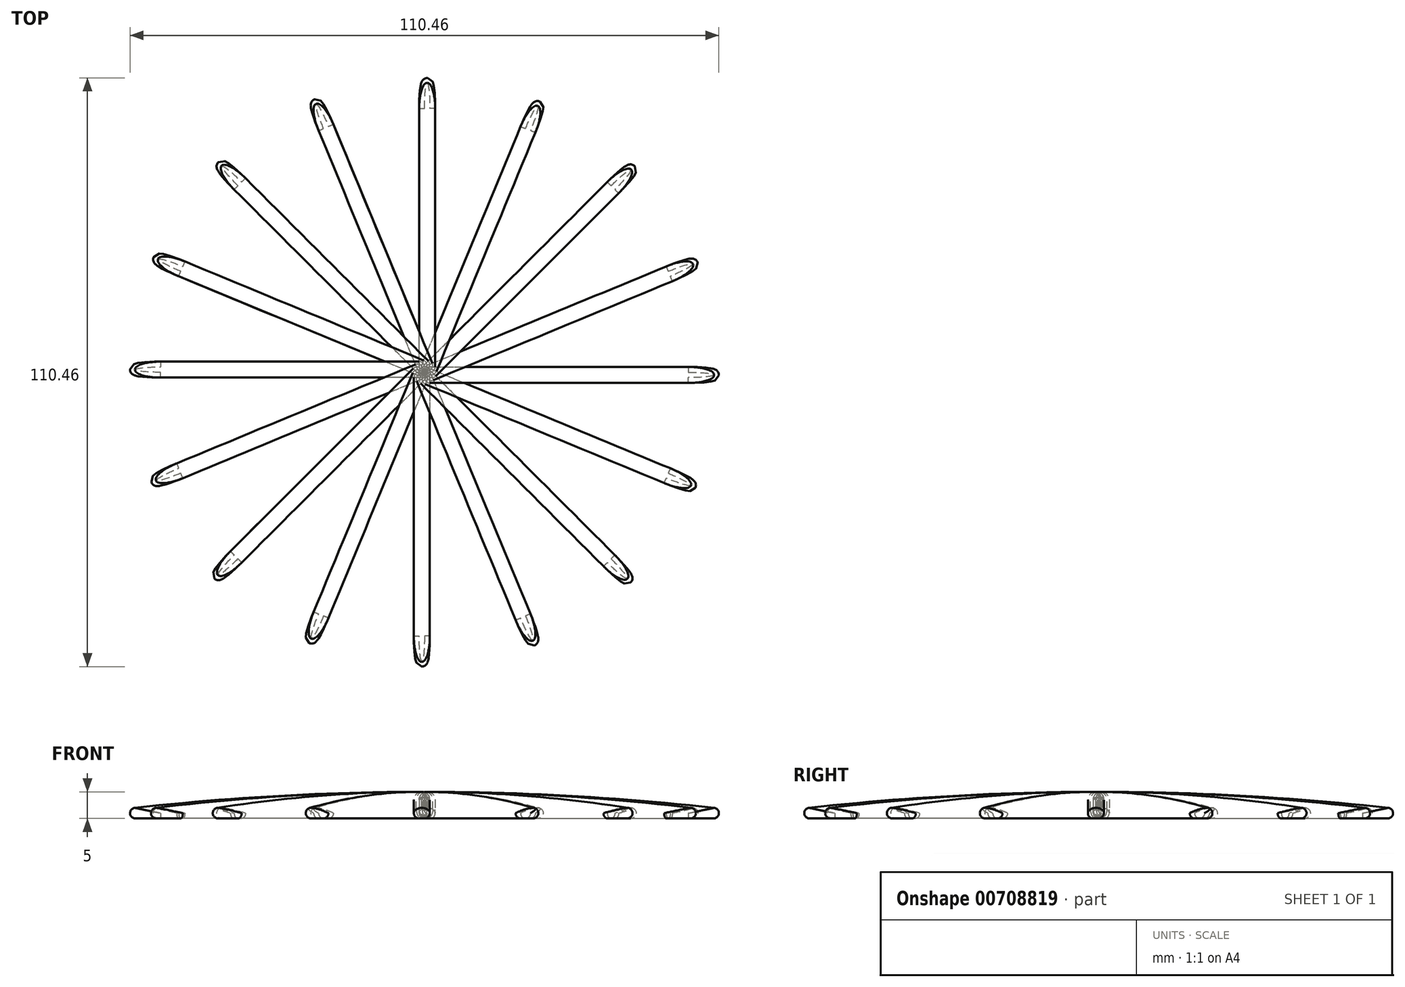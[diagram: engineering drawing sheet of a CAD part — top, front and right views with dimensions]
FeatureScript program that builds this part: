
annotation { "Feature Type Name" : "Feature", "Feature Type Description" : "" }
export const myFeature = defineFeature(function(context is Context, id is Id, definition is map)
    precondition{}
    {
        {
            var Q0;
            Q0=qCreatedBy(makeId("Top.planeOp"),FACE);
            var sketch = newSketch(context, id + "F0", { "sketchPlane" : qUnion([Q0])});
            skLineSegment(sketch, "E0.bottom", {"start": v(0, -0.98) * mm, "end": v(70, -0.98) * mm});
            skLineSegment(sketch, "E0.top", {"start": v(0, 2.02) * mm, "end": v(70, 2.02) * mm});
            skLineSegment(sketch, "E0.left", {"start": v(0, -0.98) * mm, "end": v(0, 2.02) * mm});
            skLineSegment(sketch, "E0.right", {"start": v(70, -0.98) * mm, "end": v(70, 2.02) * mm});
            skSolve(sketch);
        }
        {
            var Q0;
            Q0=makeQuery(id+"F0.imprint","IMPRINT",FACE,{"disambiguationData":[TD([[makeQuery(id+"F0.imprint","IMPRINT",EDGE,{"derivedFrom":sQuery(id+"F0.wireOp",EDGE,"E0.bottom")}),1.0]])]});
            extrude(context, id + "F1", {"entities" : qUnion([Q0]), "depth" : 5 * mm, "offsetDistance" : 25 * mm});
        }
        {
            var Q0;
            Q0=makeQuery(id+"F1.opExtrude","CAP_EDGE",EDGE,{"disambiguationData":[OSD([sQuery(id+"F0.wireOp",EDGE,"E0.right")])],"isStart":false});
            fillet(context, id + "F2", {"entities" : qUnion([Q0]), "radius" : 492 * mm, "tangentPropagation" : true, "allowEdgeOverflow" : false});
        }
        {
            var Q0;
            Q0=makeQuery(id+"F2.opFillet","BLEND_EDGE",EDGE,{"blendedFrom":[makeQuery(id+"F1.opExtrude","CAP_EDGE",EDGE,{"disambiguationData":[OSD([sQuery(id+"F0.wireOp",EDGE,"E0.right")])],"isStart":false}),makeQuery(id+"F1.opExtrude","SWEPT_FACE",FACE,{"disambiguationData":[OSD([sQuery(id+"F0.wireOp",EDGE,"E0.bottom")])]})],"blendedInto":[makeQuery(id+"F1.opExtrude","SWEPT_FACE",FACE,{"disambiguationData":[OSD([sQuery(id+"F0.wireOp",EDGE,"E0.bottom")])]})]});
            fillet(context, id + "F3", {"entities" : qUnion([Q0]), "radius" : 1.5 * mm, "tangentPropagation" : true, "allowEdgeOverflow" : false});
        }
        {
            var Q0;
            Q0=makeQuery(id+"F2.opFillet","BLEND_EDGE",EDGE,{"blendedFrom":[makeQuery(id+"F1.opExtrude","CAP_EDGE",EDGE,{"disambiguationData":[OSD([sQuery(id+"F0.wireOp",EDGE,"E0.right")])],"isStart":false}),makeQuery(id+"F1.opExtrude","SWEPT_FACE",FACE,{"disambiguationData":[OSD([sQuery(id+"F0.wireOp",EDGE,"E0.top")])]})],"blendedInto":[makeQuery(id+"F1.opExtrude","SWEPT_FACE",FACE,{"disambiguationData":[OSD([sQuery(id+"F0.wireOp",EDGE,"E0.top")])]})]});
            fillet(context, id + "F4", {"entities" : qUnion([Q0]), "radius" : 1.5 * mm, "tangentPropagation" : true, "allowEdgeOverflow" : false});
        }
        {
            var Q0;
            Q0=makeQuery(id+"F1.opExtrude","CAP_EDGE",EDGE,{"disambiguationData":[OSD([sQuery(id+"F0.wireOp",EDGE,"E0.left")])],"isStart":true});
            fillet(context, id + "F5", {"entities" : qUnion([Q0]), "radius" : 1.69 * mm, "tangentPropagation" : true, "allowEdgeOverflow" : false});
        }
        {
            var Q0;
            Q0=makeQuery(id+"F1.opExtrude","CAP_EDGE",EDGE,{"disambiguationData":[OSD([sQuery(id+"F0.wireOp",EDGE,"E0.top")])],"isStart":true});
            fillet(context, id + "F6", {"entities" : qUnion([Q0]), "radius" : 1 * mm, "tangentPropagation" : true, "allowEdgeOverflow" : false});
        }
        {
            var Q0;
            Q0=makeQuery(id+"F1.opExtrude","SWEPT_BODY",BODY,{"disambiguationData":[OSD([sQuery(id+"F0.wireOp",EDGE,"E0.bottom"),sQuery(id+"F0.wireOp",EDGE,"E0.top"),sQuery(id+"F0.wireOp",EDGE,"E0.left"),sQuery(id+"F0.wireOp",EDGE,"E0.right")])]});
            var Q1;
            {var subQ0=sQuery(id+"F0.wireOp",EDGE,"E0.left");Q1=makeQuery(id+"F6.opFillet","BLEND_EDGE",EDGE,{"blendedFrom":[makeQuery(id+"F1.opExtrude","SWEPT_EDGE",EDGE,{"disambiguationData":[OSD([sQuery(id+"F0.wireOp",EDGE,"E0.top"),subQ0])]}),makeQuery(id+"F1.opExtrude","SWEPT_FACE",FACE,{"disambiguationData":[OSD([subQ0])]})],"blendedInto":[makeQuery(id+"F1.opExtrude","SWEPT_FACE",FACE,{"disambiguationData":[OSD([subQ0])]})]});}
            circularPattern(context, id + "F7", {"entities" : qUnion([Q0]), "axis" : qUnion([Q1]), "angle" : 360 * degree, "instanceCount" : 16, "equalSpace" : true});
        }
    });
